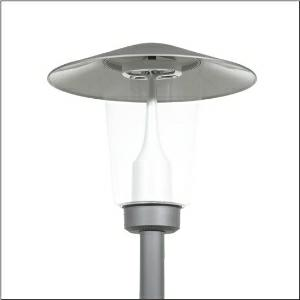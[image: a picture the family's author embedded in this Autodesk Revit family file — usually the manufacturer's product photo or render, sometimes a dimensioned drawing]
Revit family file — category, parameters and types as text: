
# Revit family: pilzleuchte_iq___st1_2a_5xa5235af14h_f6cb
name_source: partatom
category: Lighting Fixtures
units: mm (PartAtom-declared; Revit-internal decimal feet)

## family parameters
Cut with Voids When Loaded = No
Host = Face
Light Source = No
Part Type = Normal
Room Calculation Point = No
Round Connector Dimension = Use Diameter
Shared = No

## types (1)
- --- (1 x LED, 1550 lm, 12.9 W, 2200K)
    Apparent Load = 13 VA
    CIE Flux Codes = 24 61 93 98 100
    Color Rendering = 70
    Color Temperature = 2200K
    Default Elevation = 1800 mm
    Description = Mushroom Luminaire iQ, mast luminaire, Module 540 iQ-SR, primary light control with 3 zone facetted reflector, of plastic, silver coated, highly specular, structured, primary optical cover: cover, of PMMA, transparent, light distribution: ST1.2a, light emission: direct distribution, primary light characteristic: asymmetric, installation type: post-top, LED, High Power LED, rated luminous flux: 1.550lm, luminous efficacy: 120lm/W, light colour: 722, colour temperature: 2200K, control gear: iQ Street-Remote, control: pre-setting: logarithmic dimming characteristic, Street-Remote, Auto-Match, Temp-Guard, Lumen-Switch, Night-Set, Smart-Wire, Light-Fading, Desk-Remote (wireless, voltage-free reading and setting of iQ features in the workshop via application-optimized NFC function/RFID function), optimised constant luminous flux control (CLO 2.0), with terminal, 6-pole, max. 2.5mm², mains connection: 230..240V, AC, 50/60Hz, start of lifetime: 13W, end of service life: 13W, reduction: 6W, luminaire housing, upper part, of glass-fibre reinforced polyester, coated, Siteco® metallic grey (DB 702S), diameter: 650mm, height: 586mm, spigot size: d x l = 76 x 70mm (post-top) | with reducer (optional accessory) 60 x 70mm, mounting height: 3..5m, post-top mast mounting element, of diecast aluminium, coated, Siteco® metallic grey (DB 702S), Module 540 iQ-SR, traffic white (RAL 9016), equipment: standard, protection rating (complete): IP65, insulation class (complete): insulation class II (safety insulation), certification: CE, ENEC, VDE, packaging unit: 1 piece

Light Distribution: ST1.2a
    Height = 586 mm
    Lamp = 1 x LED
    Lamp Light Flux = 1550 lm
    Lamp Power = 12.9 W
    Lamp count = 1
    Length = 650 mm
    Luminous efficacy = 120 lm/W
    Manufacturer = Siteco
    ModVariant = No
    Model = 5XA5235AF14H
    Number of Poles = 1
    OnlyDefault = Yes
    Power Factor = 1
    Product Name = Pilzleuchte iQ | ST1.2a
    Product group = mast luminaire | pylon top
    ProductGroupID = 6100
    Protection Class = Protection class II
    Protection Degree = IP 65
    RLX_Detail_Level = 1
    RLX_Emergency_Light_Flux = 0 lm
    RLX_Emergency_Type = 0
    RLX_Emergency_Type_DB = No
    RlxData = <blob elided: 124873 chars, md5=e2c366b5>
    Socket = socket
    Standby Power = 0 W
    System Light Flux = 1550 lm
    System Power = 13 W
    Type Comments = factory setting: luminous flux: 100 % | dim-lin: 254 | 516 mA
    Type Image = l_1006077.jpg
    URL = http://relux.com
    VarID = @adj_160822
    Voltage = 0 V
    Weight = 0.00 kg
    Width = 0 mm  [stored 0 ft]

note: [stored X ft] marks values corroborated as IEEE doubles in the binary element streams (Revit-internal decimal feet)

## geometry (parser evidence)
native form markers: Blend x4, Sweep x11
no freeform markers — native parametric forms only
